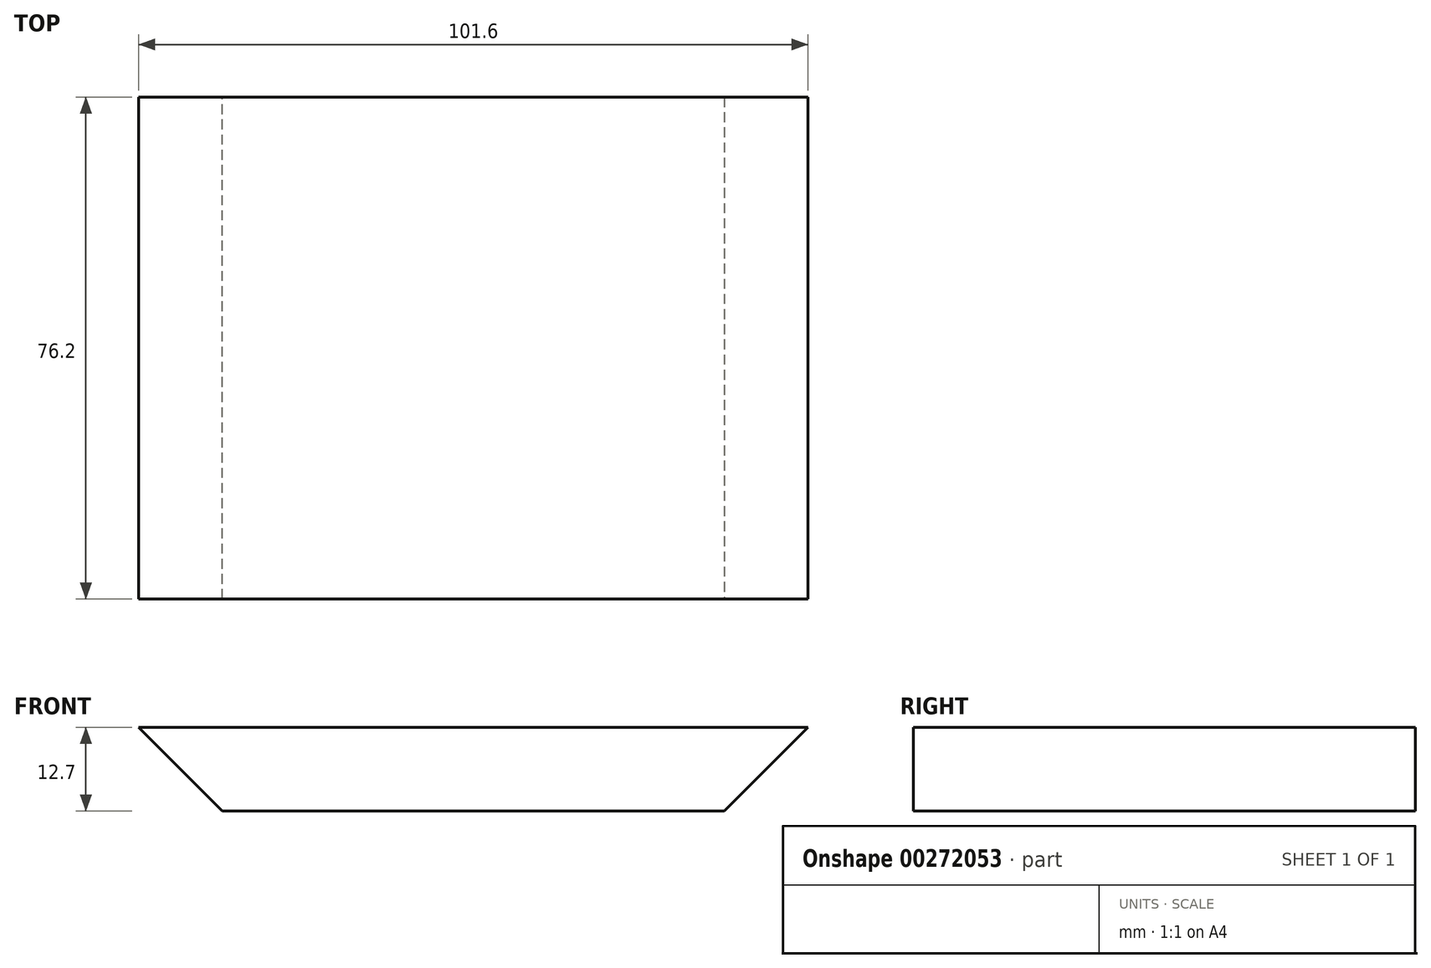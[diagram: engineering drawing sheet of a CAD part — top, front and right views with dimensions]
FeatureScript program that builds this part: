
annotation { "Feature Type Name" : "Feature", "Feature Type Description" : "" }
export const myFeature = defineFeature(function(context is Context, id is Id, definition is map)
    precondition{}
    {
        {
            var Q0;
            Q0=qCreatedBy(makeId("Top.planeOp"),FACE);
            var sketch = newSketch(context, id + "F0", { "sketchPlane" : qUnion([Q0])});
            skLineSegment(sketch, "E0.bottom", {"start": v(-53.82, 34.24) * mm, "end": v(47.78, 34.24) * mm});
            skLineSegment(sketch, "E0.top", {"start": v(-53.82, -41.96) * mm, "end": v(47.78, -41.96) * mm});
            skLineSegment(sketch, "E0.left", {"start": v(-53.82, 34.24) * mm, "end": v(-53.82, -41.96) * mm});
            skLineSegment(sketch, "E0.right", {"start": v(47.78, 34.24) * mm, "end": v(47.78, -41.96) * mm});
            skSolve(sketch);
        }
        {
            var Q0;
            Q0=makeQuery(id+"F0.imprint","IMPRINT",FACE,{"disambiguationData":[TD([[makeQuery(id+"F0.imprint","IMPRINT",EDGE,{"derivedFrom":sQuery(id+"F0.wireOp",EDGE,"E0.bottom")}),-1.0]])]});
            extrude(context, id + "F1", {"entities" : qUnion([Q0]), "depth" : 12.7 * mm});
        }
        {
            var Q0;
            Q0=makeQuery(id+"F1.opExtrude","CAP_EDGE",EDGE,{"disambiguationData":[OSD([sQuery(id+"F0.wireOp",EDGE,"E0.right")])],"isStart":true});
            var Q1;
            Q1=makeQuery(id+"F1.opExtrude","CAP_EDGE",EDGE,{"disambiguationData":[OSD([sQuery(id+"F0.wireOp",EDGE,"E0.left")])],"isStart":true});
            chamfer(context, id + "F2", {"entities" : qUnion([Q0, Q1]), "width" : 12.7 * mm, "tangentPropagation" : true});
        }
    });
